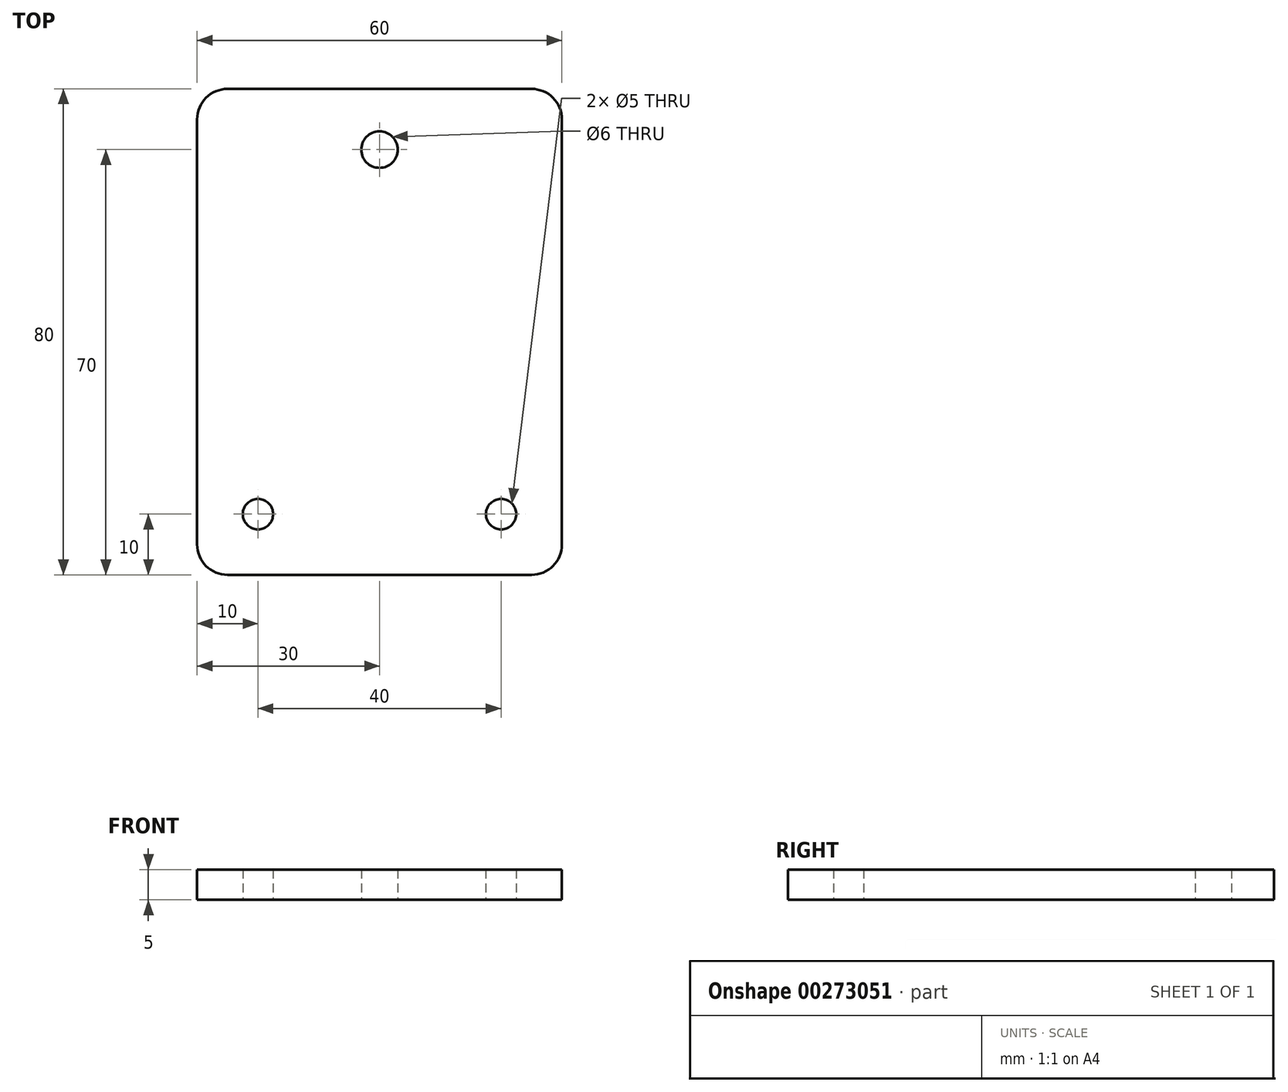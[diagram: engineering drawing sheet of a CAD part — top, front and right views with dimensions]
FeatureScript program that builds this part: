
annotation { "Feature Type Name" : "Feature", "Feature Type Description" : "" }
export const myFeature = defineFeature(function(context is Context, id is Id, definition is map)
    precondition{}
    {
        {
            var Q0;
            Q0=qCreatedBy(makeId("Top.planeOp"),FACE);
            var sketch = newSketch(context, id + "F0", { "sketchPlane" : qUnion([Q0])});
            skLineSegment(sketch, "E0.bottom", {"start": v(0, 0) * mm, "end": v(60, 0) * mm});
            skLineSegment(sketch, "E0.top", {"start": v(0, 80) * mm, "end": v(60, 80) * mm});
            skLineSegment(sketch, "E0.left", {"start": v(0, 0) * mm, "end": v(0, 80) * mm});
            skLineSegment(sketch, "E0.right", {"start": v(60, 0) * mm, "end": v(60, 80) * mm});
            skCircle(sketch, "E1", {"center": v(30, 70) * mm, "radius": 3 * mm});
            skPoint(sketch, "E1.centerSnap0", {"position": v(30, 80) * mm});
            skCircle(sketch, "E2", {"center": v(10, 10) * mm, "radius": 2.5 * mm});
            skCircle(sketch, "E3", {"center": v(50, 10) * mm, "radius": 2.5 * mm});
            skSolve(sketch);
        }
        {
            var Q0;
            Q0 = qSketchRegion(id + "F0", true);
            extrude(context, id + "F1", {"entities" : qUnion([Q0]), "depth" : 5 * mm});
        }
        {
            var Q0;
            Q0=makeQuery(id+"F1.opExtrude","SWEPT_EDGE",EDGE,{"disambiguationData":[OSD([sQuery(id+"F0.wireOp",EDGE,"E0.top"),sQuery(id+"F0.wireOp",EDGE,"E0.right")])]});
            var Q1;
            Q1=makeQuery(id+"F1.opExtrude","SWEPT_EDGE",EDGE,{"disambiguationData":[OSD([sQuery(id+"F0.wireOp",EDGE,"E0.top"),sQuery(id+"F0.wireOp",EDGE,"E0.left")])]});
            var Q2;
            Q2=makeQuery(id+"F1.opExtrude","SWEPT_EDGE",EDGE,{"disambiguationData":[OSD([sQuery(id+"F0.wireOp",EDGE,"E0.bottom"),sQuery(id+"F0.wireOp",EDGE,"E0.left")])]});
            var Q3;
            Q3=makeQuery(id+"F1.opExtrude","SWEPT_EDGE",EDGE,{"disambiguationData":[OSD([sQuery(id+"F0.wireOp",EDGE,"E0.bottom"),sQuery(id+"F0.wireOp",EDGE,"E0.right")])]});
            fillet(context, id + "F2", {"entities" : qUnion([Q0, Q1, Q2, Q3]), "radius" : 5 * mm, "tangentPropagation" : true, "allowEdgeOverflow" : false});
        }
    });
